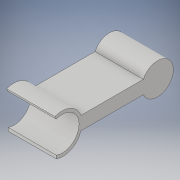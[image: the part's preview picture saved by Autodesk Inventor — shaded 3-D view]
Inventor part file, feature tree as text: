
AUTODESK INVENTOR PART (.ipt)
format: ipt  version: 2018 (Build 220112000, 112)  size: 109,056 bytes
history: native  units: in
note: dims shown in document units (in); Inventor stores cm internally (conversion verified against a paired STEP export)
features: extrude x1, sketch x1
ambient origin geometry x8: Origin, YZ Plane, XZ Plane, XY Plane, X Axis, Y Axis, Z Axis, Center Point
bodies: Body1 (feature_tree)
feature tree (2):
  extrude  "Extrusion3"  Depth=0.375in
  sketch  "Sketch1"  dims[d12=0.025in d13=0.025in d17=0.375in d18=0.0in]
